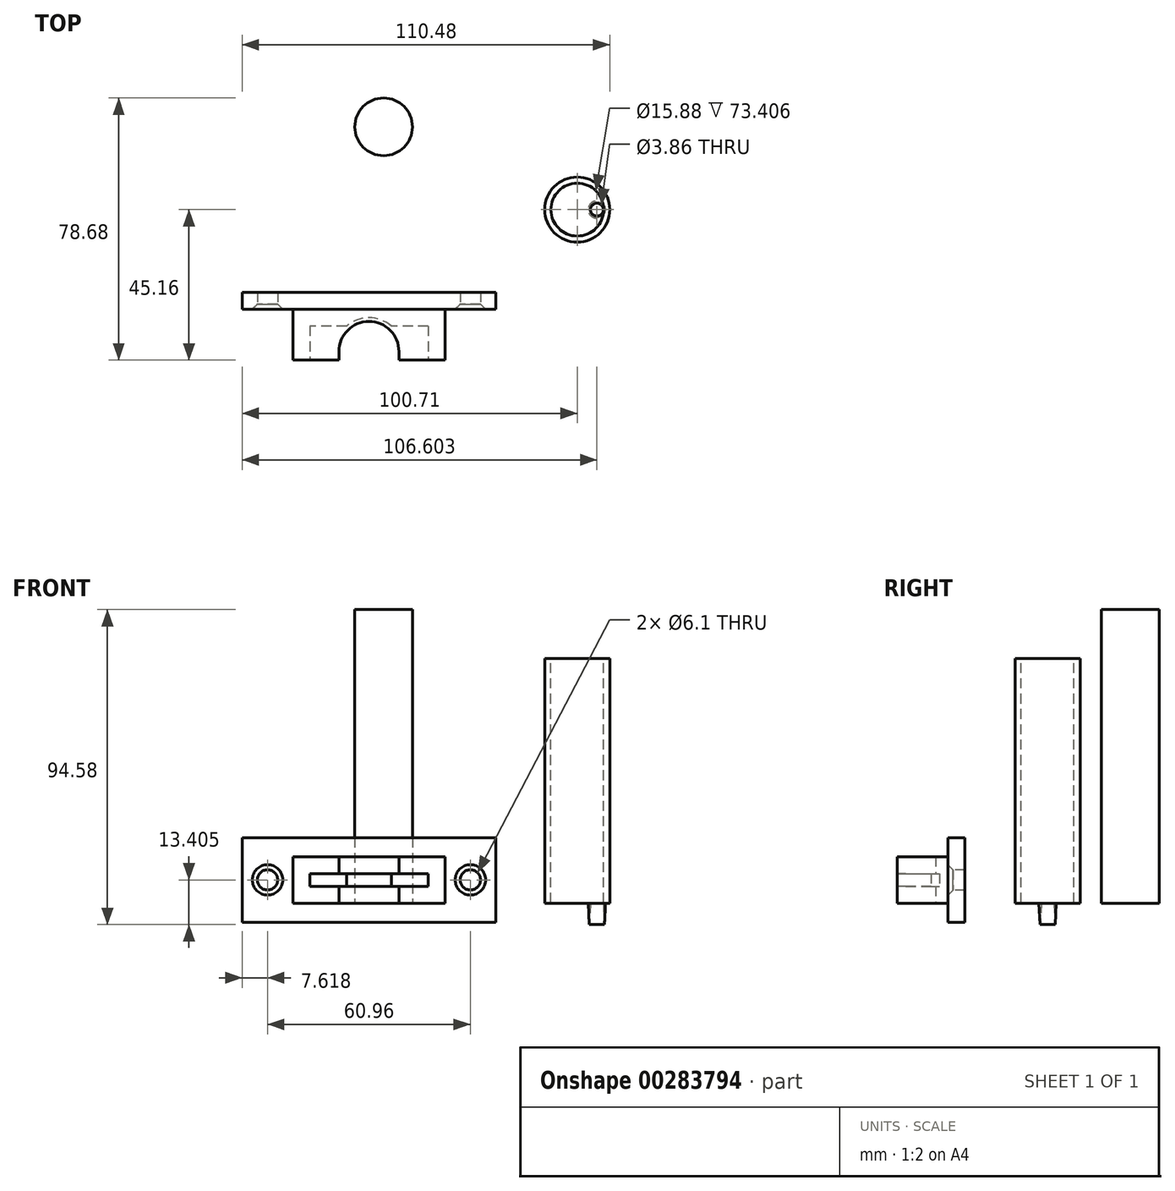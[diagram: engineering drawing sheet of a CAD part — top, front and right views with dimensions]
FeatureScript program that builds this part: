
annotation { "Feature Type Name" : "Feature", "Feature Type Description" : "" }
export const myFeature = defineFeature(function(context is Context, id is Id, definition is map)
    precondition{}
    {
        {
            var Q0;
            Q0=qCreatedBy(makeId("Top.planeOp"),FACE);
            var sketch = newSketch(context, id + "F0", { "sketchPlane" : qUnion([Q0])});
            skCircle(sketch, "E0", {"center": v(0, 0) * mm, "radius": 9.77 * mm});
            skCircle(sketch, "E1", {"center": v(5.9, 0) * mm, "radius": 2.6 * mm});
            skCircle(sketch, "E2", {"center": v(5.9, 0) * mm, "radius": 1.93 * mm});
            skSolve(sketch);
        }
        {
            var Q0;
            Q0=makeQuery(id+"F0.imprint","IMPRINT",FACE,{"disambiguationData":[TD([[makeQuery(id+"F0.imprint","IMPRINT",EDGE,{"derivedFrom":sQuery(id+"F0.wireOp",EDGE,"E0")}),1.0]])]});
            var Q1;
            Q1=makeQuery(id+"F0.imprint","IMPRINT",FACE,{"disambiguationData":[TD([[makeQuery(id+"F0.imprint","IMPRINT",EDGE,{"derivedFrom":sQuery(id+"F0.wireOp",EDGE,"E2")}),1.0]])]});
            var Q2;
            Q2=makeQuery(id+"F0.imprint","IMPRINT",FACE,{"disambiguationData":[TD([[makeQuery(id+"F0.imprint","IMPRINT",EDGE,{"derivedFrom":sQuery(id+"F0.wireOp",EDGE,"E1")}),1.0]])]});
            extrude(context, id + "F1", {"entities" : qUnion([Q0, Q1, Q2]), "depth" : 73.53 * mm});
        }
        {
            var Q0;
            Q0=makeQuery(id+"F1.opExtrude","CAP_FACE",FACE,{"disambiguationData":[OSD([sQuery(id+"F0.wireOp",EDGE,"E0")])],"isStart":false});
            var sketch = newSketch(context, id + "F2", { "sketchPlane" : qUnion([Q0])});
            skCircle(sketch, "E3", {"center": v(0, 0) * mm, "radius": 7.94 * mm});
            skSolve(sketch);
        }
        {
            var Q0;
            Q0=makeQuery(id+"F2.imprint","IMPRINT",FACE,{"disambiguationData":[TD([[makeQuery(id+"F2.imprint","IMPRINT",EDGE,{"derivedFrom":sQuery(id+"F2.wireOp",EDGE,"E3")}),1.0]])]});
            extrude(context, id + "F3", {"entities" : qUnion([Q0]), "operationType" : NewBodyOperationType.REMOVE, "oppositeDirection" : true, "depth" : 73.4 * mm});
        }
        {
            var Q0;
            Q0=makeQuery(id+"F0.imprint","IMPRINT",FACE,{"disambiguationData":[TD([[makeQuery(id+"F0.imprint","IMPRINT",EDGE,{"derivedFrom":sQuery(id+"F0.wireOp",EDGE,"E1")}),1.0]])]});
            extrude(context, id + "F4", {"entities" : qUnion([Q0]), "operationType" : NewBodyOperationType.ADD, "oppositeDirection" : true, "depth" : 12.7 * mm, "hasDraft" : true, "draftAngle" : 3 * degree, "draftPullDirection" : true});
        }
        {
            var Q0;
            Q0=makeQuery(id+"F0.imprint","IMPRINT",FACE,{"disambiguationData":[TD([[makeQuery(id+"F0.imprint","IMPRINT",EDGE,{"derivedFrom":sQuery(id+"F0.wireOp",EDGE,"E2")}),1.0]])]});
            extrude(context, id + "F5", {"entities" : qUnion([Q0]), "operationType" : NewBodyOperationType.REMOVE, "depth" : 25.4 * mm});
        }
        {
            var Q0;
            Q0=qCreatedBy(makeId("Top.planeOp"),FACE);
            var sketch = newSketch(context, id + "F6", { "sketchPlane" : qUnion([Q0])});
            skCircle(sketch, "E4", {"center": v(-58.19, 24.86) * mm, "radius": 8.66 * mm});
            skSolve(sketch);
        }
        {
            var Q0;
            Q0=qSketchRegion(id+"F6",true);
            extrude(context, id + "F7", {"entities" : qUnion([Q0]), "depth" : 88.16 * mm});
        }
        {
            var Q0;
            Q0=qCreatedBy(makeId("Top.planeOp"),FACE);
            var sketch = newSketch(context, id + "F8", { "sketchPlane" : qUnion([Q0])});
            skCircle(sketch, "E5", {"center": v(-62.61, -42.62) * mm, "radius": 9.02 * mm});
            skCircle(sketch, "E6", {"center": v(-62.61, -42.62) * mm, "radius": 10.16 * mm});
            skLineSegment(sketch, "E7.top", {"start": v(-39.75, -29.92) * mm, "end": v(-85.47, -29.92) * mm});
            skLineSegment(sketch, "E7.left", {"start": v(-39.75, -45.16) * mm, "end": v(-39.75, -29.92) * mm});
            skLineSegment(sketch, "E7.right", {"start": v(-85.47, -45.16) * mm, "end": v(-85.47, -29.92) * mm});
            skPoint(sketch, "E8", {"position": v(-62.61, -45.16) * mm});
            skLineSegment(sketch, "E9", {"start": v(-85.47, -45.16) * mm, "end": v(-39.75, -45.16) * mm});
            skLineSegment(sketch, "E10", {"start": v(-72.77, -42.62) * mm, "end": v(-72.77, -45.16) * mm});
            skLineSegment(sketch, "E11", {"start": v(-52.45, -42.62) * mm, "end": v(-52.45, -45.16) * mm});
            skLineSegment(sketch, "E12.bottom", {"start": v(-80.4, -45.16) * mm, "end": v(-44.83, -45.16) * mm});
            skLineSegment(sketch, "E12.top", {"start": v(-80.4, -35) * mm, "end": v(-44.83, -35) * mm});
            skLineSegment(sketch, "E12.left", {"start": v(-80.4, -45.16) * mm, "end": v(-80.4, -35) * mm});
            skLineSegment(sketch, "E12.right", {"start": v(-44.83, -45.16) * mm, "end": v(-44.83, -35) * mm});
            skLineSegment(sketch, "E13", {"start": v(-71.63, -42.62) * mm, "end": v(-71.63, -45.16) * mm, "construction": true});
            skLineSegment(sketch, "E14", {"start": v(-53.6, -42.62) * mm, "end": v(-53.6, -45.16) * mm, "construction": true});
            skLineSegment(sketch, "E15.bottom", {"start": v(-71.63, -42.62) * mm, "end": v(-53.6, -42.62) * mm});
            skLineSegment(sketch, "E15.top", {"start": v(-71.63, -45.16) * mm, "end": v(-53.6, -45.16) * mm});
            skLineSegment(sketch, "E15.left", {"start": v(-71.63, -42.62) * mm, "end": v(-71.63, -45.16) * mm});
            skLineSegment(sketch, "E15.right", {"start": v(-53.6, -42.62) * mm, "end": v(-53.6, -45.16) * mm});
            skSolve(sketch);
        }
        {
            var Q0;
            {var subQ1=sQuery(id+"F8.wireOp",EDGE,"E7.right");Q0=makeQuery(id+"F8.imprint","IMPRINT",FACE,{"disambiguationData":[TD([[makeQuery(id+"F8.imprint","IMPRINT",EDGE,{"derivedFrom":subQ1}),-1.0]])]});}
            var Q1;
            {var subQ1=sQuery(id+"F8.wireOp",EDGE,"E7.left");Q1=makeQuery(id+"F8.imprint","IMPRINT",FACE,{"disambiguationData":[TD([[makeQuery(id+"F8.imprint","IMPRINT",EDGE,{"derivedFrom":subQ1}),1.0]])]});}
            var Q2;
            {var subQ0=sQuery(id+"F8.wireOp",EDGE,"E10");Q2=makeQuery(id+"F8.imprint","IMPRINT",FACE,{"disambiguationData":[TD([[makeQuery(id+"F8.imprint","IMPRINT",EDGE,{"derivedFrom":subQ0}),1.0]])]});}
            var Q3;
            {var subQ0=sQuery(id+"F8.wireOp",EDGE,"E11");Q3=makeQuery(id+"F8.imprint","IMPRINT",FACE,{"disambiguationData":[TD([[makeQuery(id+"F8.imprint","IMPRINT",EDGE,{"derivedFrom":subQ0}),-1.0]])]});}
            var Q4;
            {var subQ8=sQuery(id+"F8.wireOp",EDGE,"b746b15b-b173-4421-9281-08ae0f6e52980.MirrorCS");Q4=makeQuery(id+"F8.imprint","IMPRINT",FACE,{"disambiguationData":[TD([[makeQuery(id+"F8.imprint","IMPRINT",EDGE,{"derivedFrom":subQ8}),1.0]])]});}
            var Q5;
            {var subQ1=sQuery(id+"F8.wireOp",EDGE,"E10");Q5=makeQuery(id+"F8.imprint","IMPRINT",FACE,{"disambiguationData":[TD([[makeQuery(id+"F8.imprint","IMPRINT",EDGE,{"derivedFrom":subQ1}),-1.0]])]});}
            var Q6;
            {var subQ1=sQuery(id+"F8.wireOp",EDGE,"E11");Q6=makeQuery(id+"F8.imprint","IMPRINT",FACE,{"disambiguationData":[TD([[makeQuery(id+"F8.imprint","IMPRINT",EDGE,{"derivedFrom":subQ1}),1.0]])]});}
            var Q7;
            {var subQ0=sQuery(id+"F8.wireOp",EDGE,"E12.top");var subQ1=sQuery(id+"F8.wireOp",EDGE,"E5");var subQ2=makeQuery(id+"F8.imprint","INTERSECT",VERTEX,{"disambiguationData":[OD(0.0)],"derivedFrom":[subQ1,subQ0]});Q7=makeQuery(id+"F8.imprint","IMPRINT",FACE,{"disambiguationData":[TD([[makeQuery(id+"F8.imprint","IMPRINT",EDGE,{"disambiguationData":[TD([[subQ2,-1.0]])],"derivedFrom":subQ1}),-1.0]])]});}
            var Q8;
            {var subQ4=sQuery(id+"F8.wireOp",EDGE,"E12.top");var subQ6=sQuery(id+"F8.wireOp",EDGE,"E5");var subQ7=makeQuery(id+"F8.imprint","INTERSECT",VERTEX,{"disambiguationData":[OD(1.0)],"derivedFrom":[subQ6,subQ4]});Q8=makeQuery(id+"F8.imprint","IMPRINT",FACE,{"disambiguationData":[TD([[makeQuery(id+"F8.imprint","IMPRINT",EDGE,{"disambiguationData":[TD([[subQ7,-1.0]])],"derivedFrom":subQ6}),-1.0]])]});}
            var Q9;
            {var subQ0=sQuery(id+"F8.wireOp",EDGE,"E15.right");Q9=makeQuery(id+"F8.imprint","IMPRINT",FACE,{"disambiguationData":[TD([[makeQuery(id+"F8.imprint","IMPRINT",EDGE,{"derivedFrom":subQ0}),1.0]])]});}
            extrude(context, id + "F9", {"entities" : qUnion([Q0, Q1, Q2, Q3, Q4, Q5, Q6, Q7, Q8, Q9]), "depth" : 5.08 * mm});
        }
        {
            var Q0;
            {var subQ0=sQuery(id+"F8.wireOp",EDGE,"E7.right");Q0=makeQuery(id+"F8.imprint","IMPRINT",FACE,{"disambiguationData":[TD([[makeQuery(id+"F8.imprint","IMPRINT",EDGE,{"derivedFrom":subQ0}),-1.0]])]});}
            var Q1;
            {var subQ3=sQuery(id+"F8.wireOp",EDGE,"E7.left");Q1=makeQuery(id+"F8.imprint","IMPRINT",FACE,{"disambiguationData":[TD([[makeQuery(id+"F8.imprint","IMPRINT",EDGE,{"derivedFrom":subQ3}),1.0]])]});}
            extrude(context, id + "F10", {"entities" : qUnion([Q0, Q1]), "operationType" : NewBodyOperationType.ADD, "depth" : 8.9 * mm});
        }
        {
            var Q0;
            {var subQ3=sQuery(id+"F8.wireOp",EDGE,"E7.right");Q0=makeQuery(id+"F8.imprint","IMPRINT",FACE,{"disambiguationData":[TD([[makeQuery(id+"F8.imprint","IMPRINT",EDGE,{"derivedFrom":subQ3}),-1.0]])]});}
            var Q1;
            {var subQ3=sQuery(id+"F8.wireOp",EDGE,"E7.left");Q1=makeQuery(id+"F8.imprint","IMPRINT",FACE,{"disambiguationData":[TD([[makeQuery(id+"F8.imprint","IMPRINT",EDGE,{"derivedFrom":subQ3}),1.0]])]});}
            var Q2;
            {var subQ1=sQuery(id+"F8.wireOp",EDGE,"E11");Q2=makeQuery(id+"F8.imprint","IMPRINT",FACE,{"disambiguationData":[TD([[makeQuery(id+"F8.imprint","IMPRINT",EDGE,{"derivedFrom":subQ1}),1.0]])]});}
            var Q3;
            {var subQ4=sQuery(id+"F8.wireOp",EDGE,"b746b15b-b173-4421-9281-08ae0f6e52980.MirrorCS");Q3=makeQuery(id+"F8.imprint","IMPRINT",FACE,{"disambiguationData":[TD([[makeQuery(id+"F8.imprint","IMPRINT",EDGE,{"derivedFrom":subQ4}),1.0]])]});}
            var Q4;
            {var subQ0=sQuery(id+"F8.wireOp",EDGE,"E12.top");var subQ1=sQuery(id+"F8.wireOp",EDGE,"E5");var subQ2=makeQuery(id+"F8.imprint","INTERSECT",VERTEX,{"disambiguationData":[OD(0.0)],"derivedFrom":[subQ1,subQ0]});Q4=makeQuery(id+"F8.imprint","IMPRINT",FACE,{"disambiguationData":[TD([[makeQuery(id+"F8.imprint","IMPRINT",EDGE,{"disambiguationData":[TD([[subQ2,-1.0]])],"derivedFrom":subQ1}),-1.0]])]});}
            var Q5;
            {var subQ4=sQuery(id+"F8.wireOp",EDGE,"oYCFffuB-2gqM-RgqH-B8UD-AKh6t3XLDEdo");Q5=makeQuery(id+"F8.imprint","IMPRINT",FACE,{"disambiguationData":[TD([[makeQuery(id+"F8.imprint","IMPRINT",EDGE,{"derivedFrom":subQ4}),-1.0]])]});}
            var Q6;
            {var subQ1=sQuery(id+"F8.wireOp",EDGE,"E10");Q6=makeQuery(id+"F8.imprint","IMPRINT",FACE,{"disambiguationData":[TD([[makeQuery(id+"F8.imprint","IMPRINT",EDGE,{"derivedFrom":subQ1}),-1.0]])]});}
            var Q7;
            {var subQ0=sQuery(id+"F8.wireOp",EDGE,"E10");Q7=makeQuery(id+"F8.imprint","IMPRINT",FACE,{"disambiguationData":[TD([[makeQuery(id+"F8.imprint","IMPRINT",EDGE,{"derivedFrom":subQ0}),1.0]])]});}
            var Q8;
            {var subQ0=sQuery(id+"F8.wireOp",EDGE,"E11");Q8=makeQuery(id+"F8.imprint","IMPRINT",FACE,{"disambiguationData":[TD([[makeQuery(id+"F8.imprint","IMPRINT",EDGE,{"derivedFrom":subQ0}),-1.0]])]});}
            var Q9;
            {var subQ6=sQuery(id+"F8.wireOp",EDGE,"E15.left");Q9=makeQuery(id+"F8.imprint","IMPRINT",FACE,{"disambiguationData":[TD([[makeQuery(id+"F8.imprint","IMPRINT",EDGE,{"derivedFrom":subQ6}),-1.0]])]});}
            var Q10;
            {var subQ0=sQuery(id+"F8.wireOp",EDGE,"E15.right");Q10=makeQuery(id+"F8.imprint","IMPRINT",FACE,{"disambiguationData":[TD([[makeQuery(id+"F8.imprint","IMPRINT",EDGE,{"derivedFrom":subQ0}),1.0]])]});}
            extrude(context, id + "F11", {"entities" : qUnion([Q0, Q1, Q2, Q3, Q4, Q5, Q6, Q7, Q8, Q9, Q10]), "operationType" : NewBodyOperationType.ADD, "depth" : 13.97 * mm, "hasSecondDirection" : true, "secondDirectionOppositeDirection" : false, "secondDirectionDepth" : 8.9 * mm});
        }
        {
            var Q0;
            {var subQ0=sQuery(id+"F8.wireOp",EDGE,"E7.top");Q0=makeQuery(id+"F11.boolean.opBoolean","MERGE",FACE,{"derivedFrom":[makeQuery(id+"F10.boolean.opBoolean","MERGE",FACE,{"derivedFrom":[makeQuery(id+"F9.opExtrude","SWEPT_FACE",FACE,{"disambiguationData":[OSD([subQ0])]}),makeQuery(id+"F10.opExtrude","SWEPT_FACE",FACE,{"disambiguationData":[OSD([subQ0])]})]}),makeQuery(id+"F11.opExtrude","SWEPT_FACE",FACE,{"disambiguationData":[OSD([subQ0])]})]});}
            var sketch = newSketch(context, id + "F12", { "sketchPlane" : qUnion([Q0])});
            skLineSegment(sketch, "E16.bottom", {"start": v(100.71, -5.71) * mm, "end": v(24.51, -5.71) * mm});
            skLineSegment(sketch, "E16.top", {"start": v(100.71, 19.69) * mm, "end": v(24.51, 19.69) * mm});
            skLineSegment(sketch, "E16.left", {"start": v(100.71, -5.72) * mm, "end": v(100.71, 19.69) * mm});
            skLineSegment(sketch, "E16.right", {"start": v(24.51, -5.72) * mm, "end": v(24.51, 19.69) * mm});
            skPoint(sketch, "E16.middle", {"position": v(62.61, 6.99) * mm});
            skPoint(sketch, "E16.middle.positionSnap0", {"position": v(85.47, 6.99) * mm});
            skPoint(sketch, "E16.middle.positionSnap1", {"position": v(62.61, 0) * mm});
            skPoint(sketch, "E16.centerSnap0", {"position": v(85.47, 6.99) * mm});
            skPoint(sketch, "E16.centerSnap1", {"position": v(62.61, 0) * mm});
            skLineSegment(sketch, "E17", {"start": v(85.47, 6.99) * mm, "end": v(100.71, 6.99) * mm, "construction": true});
            skCircle(sketch, "E18", {"center": v(93.1, 6.99) * mm, "radius": 3.05 * mm});
            skLineSegment(sketch, "E19", {"start": v(62.61, 0) * mm, "end": v(62.61, 6.99) * mm, "construction": true});
            skCircle(sketch, "E20.MirrorC", {"center": v(32.13, 6.98) * mm, "radius": 3.05 * mm});
            skSolve(sketch);
        }
        {
            var Q0;
            Q0=makeQuery(id+"F12.imprint","IMPRINT",FACE,{"disambiguationData":[TD([[makeQuery(id+"F12.imprint","IMPRINT",EDGE,{"derivedFrom":sQuery(id+"F12.wireOp",EDGE,"E16.bottom")}),-1.0]])]});
            var Q1;
            {var subQ0=sQuery(id+"F8.wireOp",EDGE,"E7.top");Q1=makeQuery(id+"F12.imprint","IMPRINT",FACE,{"disambiguationData":[TD([[makeQuery(id+"F12.imprint","IMPRINT",EDGE,{"derivedFrom":makeQuery(id+"F9.opExtrude","CAP_EDGE",EDGE,{"disambiguationData":[OSD([subQ0])],"isStart":true})}),1.0]])]});}
            extrude(context, id + "F13", {"entities" : qUnion([Q0, Q1]), "operationType" : NewBodyOperationType.ADD, "depth" : 5.08 * mm});
        }
        {
            var Q0;
            Q0=makeQuery(id+"F13.opExtrude","CAP_EDGE",EDGE,{"disambiguationData":[OSD([sQuery(id+"F12.wireOp",EDGE,"E18")])],"isStart":true});
            var Q1;
            Q1=makeQuery(id+"F13.opExtrude","CAP_EDGE",EDGE,{"disambiguationData":[OSD([sQuery(id+"F12.wireOp",EDGE,"E20.MirrorC")])],"isStart":true});
            chamfer(context, id + "F14", {"entities" : qUnion([Q0, Q1]), "width" : 1.52 * mm, "tangentPropagation" : true});
        }
    });
